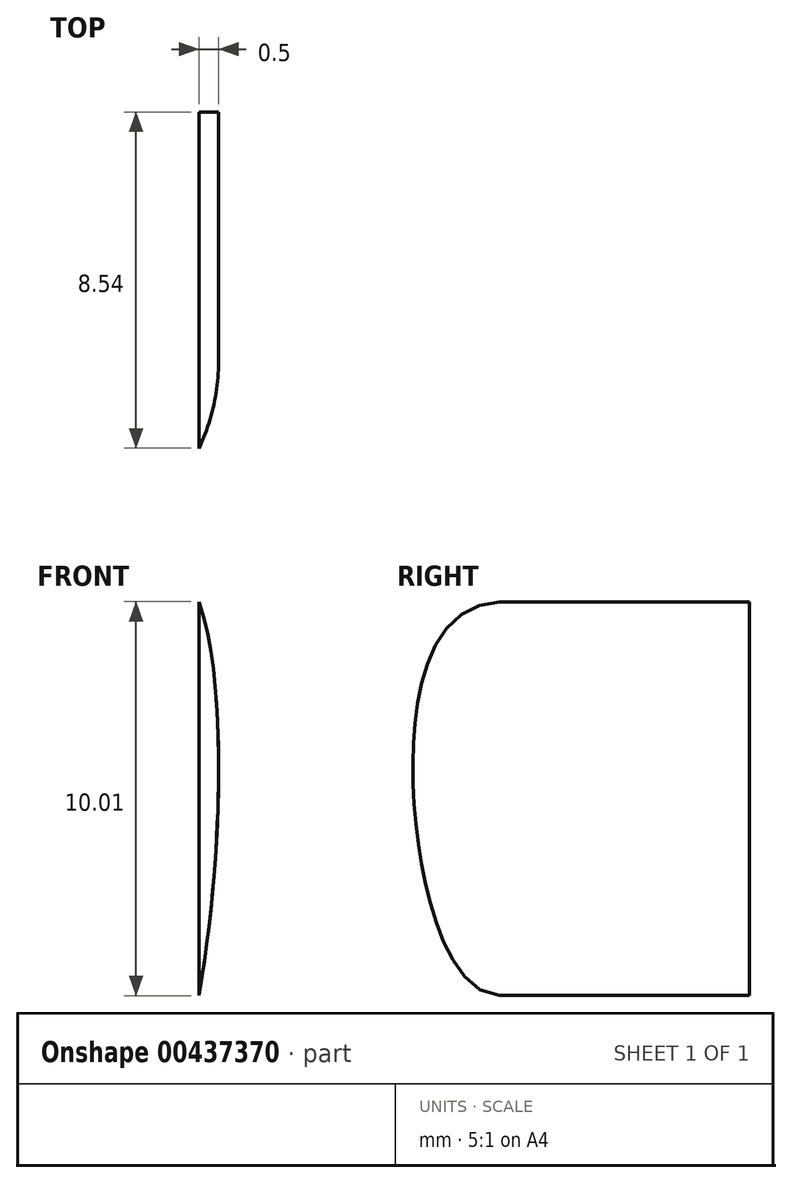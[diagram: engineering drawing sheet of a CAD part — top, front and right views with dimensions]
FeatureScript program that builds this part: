
annotation { "Feature Type Name" : "Feature", "Feature Type Description" : "" }
export const myFeature = defineFeature(function(context is Context, id is Id, definition is map)
    precondition{}
    {
        {
            var Q0;
            Q0=qCreatedBy(makeId("Front.planeOp"),FACE);
            var sketch = newSketch(context, id + "F0", { "sketchPlane" : qUnion([Q0])});
            skLineSegment(sketch, "E0", {"start": v(-35.82, 9.77) * mm, "end": v(-35.82, -7.68) * mm});
            skFitSpline(sketch, "E1", {"points": [v(-35.82, -7.68) * mm, v(-24.42, -5.58) * mm, v(-13.5, -7.68) * mm, v(0, -5.81) * mm, v(10.47, -7.68) * mm, v(20.24, -5.35) * mm, v(26.75, -7.68) * mm, v(25.35, 5.12) * mm, v(-35.82, 9.77) * mm, v(-35.82, 7.68) * mm, v(-35.82, -2.33) * mm, v(-35.82, -7.68) * mm]});
            skSolve(sketch);
        }
        {
            var Q0;
            {var subQ0=sQuery(id+"F0.wireOp",EDGE,"E1");var subQ1=sQuery(id+"F0.wireOp",EDGE,"E0");var subQ2=makeQuery(id+"F0.imprint","INTERSECT",VERTEX,{"disambiguationData":[OD(0.0)],"derivedFrom":[subQ1,subQ0]});Q0=makeQuery(id+"F0.imprint","IMPRINT",FACE,{"disambiguationData":[TD([[makeQuery(id+"F0.imprint","IMPRINT",EDGE,{"disambiguationData":[TD([[subQ2,-1.0]])],"derivedFrom":subQ1}),1.0]])]});}
            extrude(context, id + "F1", {"entities" : qUnion([Q0]), "oppositeDirection" : true, "depth" : 11.43 * mm});
        }
        {
            var Q0;
            {var subQ0=sQuery(id+"F0.wireOp",EDGE,"E1");var subQ1=sQuery(id+"F0.wireOp",EDGE,"E0");Q0=makeQuery(id+"F1.opExtrude","CAP_EDGE",EDGE,{"disambiguationData":[OSD([subQ0]),TDD([makeQuery(id+"F0.imprint","IMPRINT",EDGE,{"disambiguationData":[TD([[makeQuery(id+"F0.imprint","INTERSECT",VERTEX,{"disambiguationData":[OD(0.0)],"derivedFrom":[subQ1,subQ0]}),1.0]])],"derivedFrom":subQ0})])],"isStart":true});}
            var Q1;
            {var subQ0=sQuery(id+"F0.wireOp",EDGE,"E1");var subQ1=sQuery(id+"F0.wireOp",EDGE,"E0");Q1=makeQuery(id+"F1.opExtrude","CAP_EDGE",EDGE,{"disambiguationData":[OSD([subQ0]),TDD([makeQuery(id+"F0.imprint","IMPRINT",EDGE,{"disambiguationData":[TD([[makeQuery(id+"F0.imprint","INTERSECT",VERTEX,{"disambiguationData":[OD(0.0)],"derivedFrom":[subQ1,subQ0]}),1.0]])],"derivedFrom":subQ0})])],"isStart":true});}
            fillet(context, id + "F2", {"entities" : qUnion([Q0, Q1]), "radius" : 5.08 * mm, "tangentPropagation" : true, "allowEdgeOverflow" : false});
        }
    });
